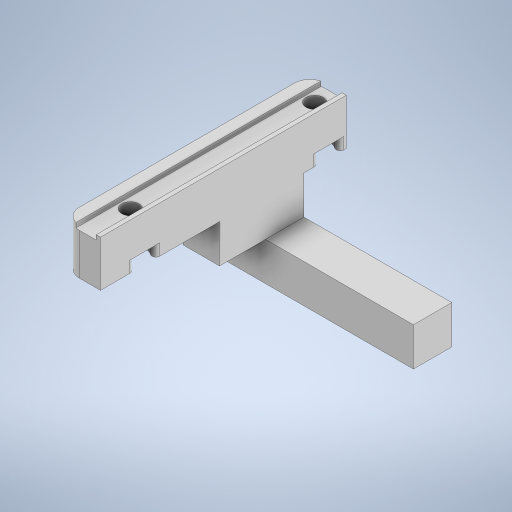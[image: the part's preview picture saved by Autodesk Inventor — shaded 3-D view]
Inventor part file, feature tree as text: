
AUTODESK INVENTOR PART (.ipt)
format: ipt  version: 2024 (Build 280153000, 153)  size: 321,536 bytes
history: native  units: in
note: dims shown in document units (in); Inventor stores cm internally (conversion verified against a paired STEP export)
features: extrude x5, sketch x5, projected_geometry x4, fillet x2
ambient origin geometry x8: Origin, YZ Plane, XZ Plane, XY Plane, X Axis, Y Axis, Z Axis, Center Point
bodies: Solid1 (feature_tree)
feature tree (16):
  extrude  "Extrusion1"  Depth=2.5197in
  extrude  "Extrusion2"  Depth=1.8898in
  extrude  "Extrusion3"  Depth=0.4724in TaperAngle=0.0deg
  fillet  "Fillet1"  Radius=0.0433in
  fillet  "Fillet2"  Radius=0.2126in
  extrude  "Extrusion19"  Depth=0.4724in TaperAngle=0.0deg
  extrude  "Extrusion20"  Depth=0.1181in TaperAngle=0.0deg
  sketch  "Sketch1"  dims[d1=0.374in d2=2.5197in]
  sketch  "Sketch2"  dims[d3=0.1772in d4=1.8898in]
  sketch  "Sketch3"  dims[d6=0.1457in d7=0.4724in d8=0.0in d9=0.0433in d10=0.2126in]
  projected_geometry  "Projected Loop2"
  projected_geometry  "Projected Loop3"
  projected_geometry  "Projected Loop4"
  projected_geometry  "Projected Loop5"
  sketch  "Sketch28"  dims[d11=0.0472in d12=0.4724in d13=0.0in]
  sketch  "Sketch29"  dims[d14=0.2953in d15=0.1181in d16=0.0in d17=0.1772in d18=0.0394in d19=0.1575in d76=0.4724in d107=0.102in d108=0.8661in d109=0.3937in d110=0.0in d111=1.8898in d112=0.3937in d113=2.3622in d114=0.3937in d115=0.3937in d116=0.0in d42=0.0197in d43=0.0344in d44=0.0197in d45=0.0344in d46=0.0in d47=0.0in d48=0.0in d49=0.0in d50=0.0in d51=0.0in d52=0.0in d53=0.0in d55=0.0197in d56=0.0344in d57=0.0197in d58=0.0344in d60=0.0197in d61=0.0344in d62=0.0197in d63=0.0344in d72=0.0197in d73=0.0344in d74=0.0197in d75=0.0344in]
